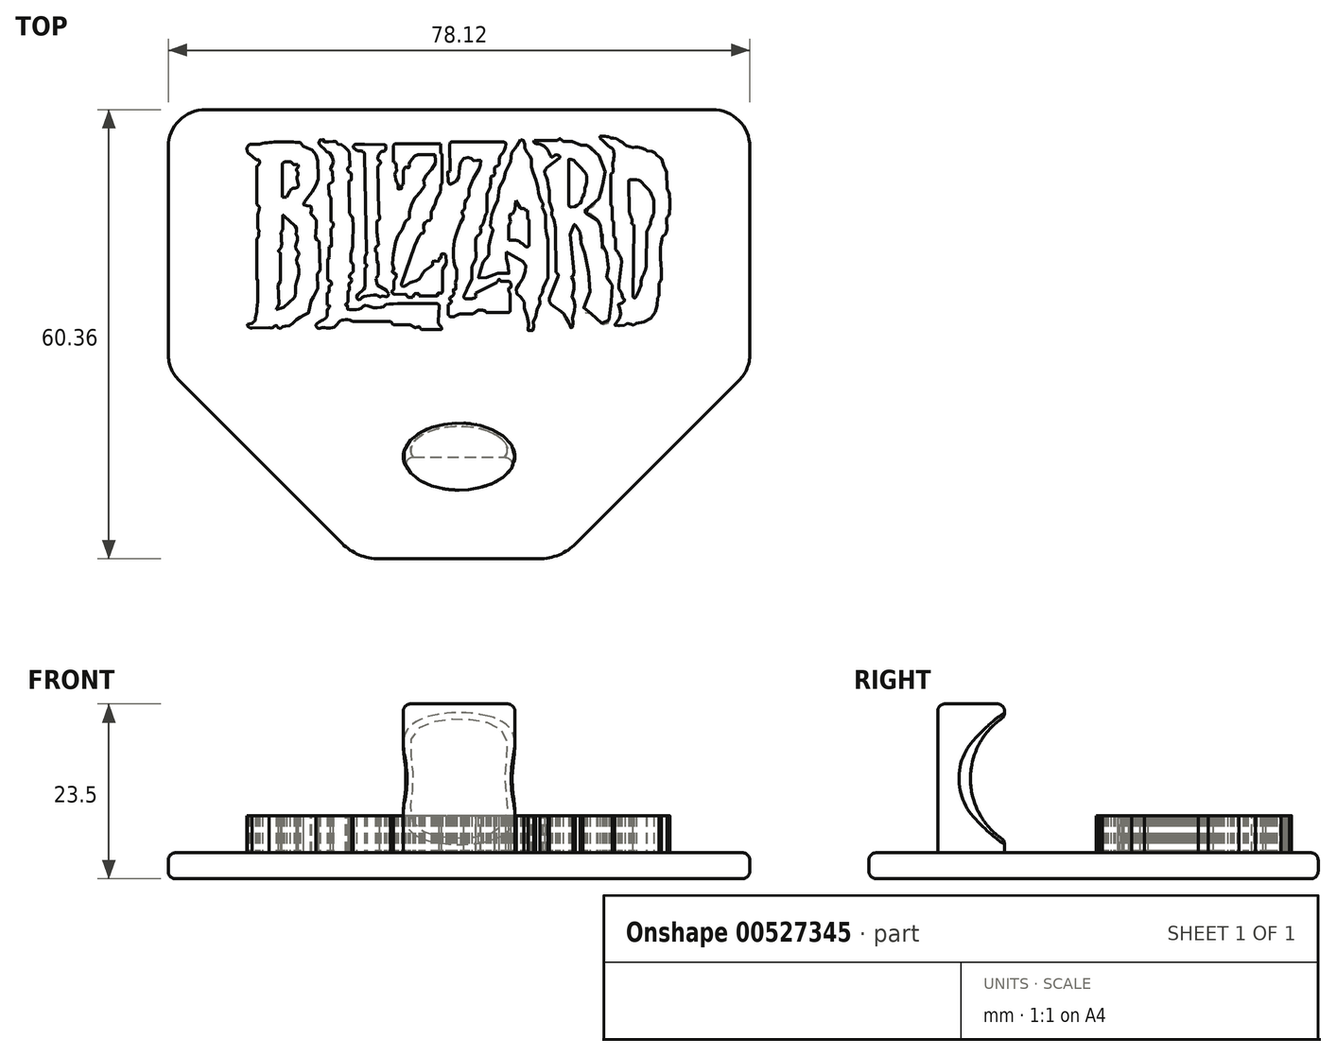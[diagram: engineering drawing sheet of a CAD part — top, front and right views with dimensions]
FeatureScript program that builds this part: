
annotation { "Feature Type Name" : "Feature", "Feature Type Description" : "" }
export const myFeature = defineFeature(function(context is Context, id is Id, definition is map)
    precondition{}
    {
        {
            var Q0;
            Q0=qCreatedBy(makeId("Top.planeOp"),FACE);
            var sketch = newSketch(context, id + "F0", { "sketchPlane" : qUnion([Q0])});
            skLineSegment(sketch, "E0", {"start": v(-31.15, 9.77) * mm, "end": v(-31.15, 4.7) * mm});
            skLineSegment(sketch, "E1", {"start": v(-27.73, 10.06) * mm, "end": v(-27.73, 5.6) * mm});
            skLineSegment(sketch, "E2", {"start": v(-27.56, -9.2) * mm, "end": v(-26.16, -7.94) * mm});
            skLineSegment(sketch, "E3", {"start": v(-16.69, 11.24) * mm, "end": v(-16.4, -1.7) * mm});
            skLineSegment(sketch, "E4", {"start": v(-21.18, 2.33) * mm, "end": v(-21.18, 5.56) * mm});
            skLineSegment(sketch, "E5", {"start": v(-12.42, 12.8) * mm, "end": v(-6.45, 12.8) * mm});
            skLineSegment(sketch, "E6", {"start": v(-5, 13.02) * mm, "end": v(2.01, 13.02) * mm});
            skLineSegment(sketch, "E7", {"start": v(-0.26, -9.88) * mm, "end": v(2.61, -9.88) * mm});
            skLineSegment(sketch, "E8", {"start": v(-12.22, -8.7) * mm, "end": v(-7.01, -8.7) * mm});
            skLineSegment(sketch, "E9", {"start": v(-11.71, -6.1) * mm, "end": v(-9.93, -0.9) * mm});
            skLineSegment(sketch, "E10", {"start": v(-14.92, 9.66) * mm, "end": v(-14.8, 3.49) * mm});
            skLineSegment(sketch, "E11", {"start": v(-9.4, 11.32) * mm, "end": v(-7.37, 11.32) * mm});
            skLineSegment(sketch, "E12", {"start": v(19.53, 1.66) * mm, "end": v(19.41, -7.54) * mm});
            skLineSegment(sketch, "E13", {"start": v(10.74, 10.42) * mm, "end": v(10.74, 4.64) * mm});
            skLineSegment(sketch, "E14", {"start": v(10.93, 0.57) * mm, "end": v(11.43, 1.89) * mm});
            skLineSegment(sketch, "E15", {"start": v(11.61, 1.83) * mm, "end": v(12.27, 0.9) * mm});
            skLineSegment(sketch, "E16", {"start": v(18.97, 7.94) * mm, "end": v(19.83, 7.94) * mm});
            skLineSegment(sketch, "E17", {"start": v(-21.66, -2.75) * mm, "end": v(-21.66, -5.44) * mm});
            skLineSegment(sketch, "E18", {"start": v(-18.23, -3.4) * mm, "end": v(-18.23, -4.42) * mm});
            skLineSegment(sketch, "E19", {"start": v(-27.68, 2.98) * mm, "end": v(-27.68, 1.32) * mm});
            skLineSegment(sketch, "E20", {"start": v(-27.5, 3.09) * mm, "end": v(-26.01, 1.7) * mm});
            skLineSegment(sketch, "E21", {"start": v(-28.3, -6.24) * mm, "end": v(-28.19, -8.73) * mm});
            skLineSegment(sketch, "E22", {"start": v(-28.3, -6.24) * mm, "end": v(-27.98, -5.72) * mm});
            skLineSegment(sketch, "E23", {"start": v(-31.22, 10.62) * mm, "end": v(-32.18, 11.42) * mm});
            skLineSegment(sketch, "E24", {"start": v(-9.07, -12.2) * mm, "end": v(-6.44, -12.2) * mm});
            skLineSegment(sketch, "E25", {"start": v(-6.66, -9.06) * mm, "end": v(-6.8, -11.02) * mm});
            skLineSegment(sketch, "E26", {"start": v(-18.19, -11.12) * mm, "end": v(-13.16, -11.12) * mm});
            skLineSegment(sketch, "E27", {"start": v(-13.16, -11.12) * mm, "end": v(-12.82, -11.53) * mm});
            skLineSegment(sketch, "E28", {"start": v(-12.82, -11.53) * mm, "end": v(-10.6, -11.53) * mm});
            skLineSegment(sketch, "E29", {"start": v(-10.6, -11.53) * mm, "end": v(-9.86, -11.92) * mm});
            skLineSegment(sketch, "E30", {"start": v(-9.22, -11.9) * mm, "end": v(-9.07, -12.2) * mm});
            skLineSegment(sketch, "E31", {"start": v(-21.68, -7.33) * mm, "end": v(-21.68, -8.9) * mm});
            skLineSegment(sketch, "E32", {"start": v(-18.92, -7.07) * mm, "end": v(-18.92, -8.47) * mm});
            skLineSegment(sketch, "E33", {"start": v(-22.76, -0.4) * mm, "end": v(-22.66, -4.23) * mm});
            skLineSegment(sketch, "E34", {"start": v(-21.16, 1.4) * mm, "end": v(-21.1, -0.86) * mm});
            skLineSegment(sketch, "E35", {"start": v(-18.8, 7.77) * mm, "end": v(-18.7, 3.44) * mm});
            skLineSegment(sketch, "E36", {"start": v(-6.26, 11.4) * mm, "end": v(-6.26, 7.46) * mm});
            skLineSegment(sketch, "E37", {"start": v(-5.23, 12.65) * mm, "end": v(-5.16, 9.13) * mm});
            skLineSegment(sketch, "E38", {"start": v(5.45, 2.52) * mm, "end": v(5.45, -0.87) * mm});
            skLineSegment(sketch, "E39", {"start": v(2.68, 1.8) * mm, "end": v(2.68, -0.2) * mm});
            skLineSegment(sketch, "E40", {"start": v(2.68, -0.2) * mm, "end": v(3.72, -0.2) * mm});
            skLineSegment(sketch, "E41", {"start": v(3.67, 5.18) * mm, "end": v(3.55, 3.97) * mm});
            skLineSegment(sketch, "E42", {"start": v(3.67, 5.18) * mm, "end": v(4.2, 4.19) * mm});
            skLineSegment(sketch, "E43", {"start": v(5.24, 3.8) * mm, "end": v(5.24, 2.67) * mm});
            skLineSegment(sketch, "E44", {"start": v(2.95, 3.31) * mm, "end": v(3.2, 3.31) * mm});
            skLineSegment(sketch, "E45", {"start": v(2.81, 2.88) * mm, "end": v(2.93, 2.3) * mm});
            skLineSegment(sketch, "E46", {"start": v(2.93, 2.3) * mm, "end": v(2.68, 1.8) * mm});
            skLineSegment(sketch, "E47", {"start": v(4.5, -0.62) * mm, "end": v(4.93, -1) * mm});
            skArc(sketch, "E48", {"start": v(4.93, -1) * mm, "mid": v(5.22, -1.07) * mm, "end": v(5.45, -0.87) * mm});
            skFitSpline(sketch, "E49", {"points": [v(3.72, -0.2) * mm, v(3.88, -0.24) * mm, v(4.03, -0.29) * mm, v(4.16, -0.37) * mm, v(4.22, -0.48) * mm, v(4.26, -0.54) * mm, v(4.34, -0.57) * mm, v(4.5, -0.62) * mm], "startDerivative": vector(1.01, -0.19) * mm, "endDerivative": vector(1.05, -0.37) * mm});
            skFitSpline(sketch, "E50", {"points": [v(2.95, 3.31) * mm, v(2.89, 3.31) * mm, v(2.84, 3.27) * mm, v(2.82, 3.17) * mm, v(2.81, 2.88) * mm], "startDerivative": vector(-0.37, 0.05) * mm, "endDerivative": vector(0, -0.8) * mm});
            skLineSegment(sketch, "E51", {"start": v(3.55, 3.97) * mm, "end": v(3.2, 3.31) * mm});
            skLineSegment(sketch, "E52", {"start": v(4.41, 4.08) * mm, "end": v(4.78, 4.08) * mm});
            skLineSegment(sketch, "E53", {"start": v(4.78, 4.08) * mm, "end": v(4.98, 3.8) * mm});
            skLineSegment(sketch, "E54", {"start": v(4.98, 3.8) * mm, "end": v(5.24, 3.8) * mm});
            skArc(sketch, "E55", {"start": v(4.2, 4.19) * mm, "mid": v(4.29, 4.1) * mm, "end": v(4.41, 4.08) * mm});
            skLineSegment(sketch, "E56", {"start": v(-27.73, 5.6) * mm, "end": v(-27.17, 5.6) * mm});
            skLineSegment(sketch, "E57", {"start": v(-27.17, 5.6) * mm, "end": v(-26.68, 6.45) * mm});
            skFitSpline(sketch, "E58", {"points": [v(-26.68, 6.45) * mm, v(-26.55, 6.63) * mm, v(-26.38, 6.75) * mm, v(-26.2, 6.8) * mm, v(-25.95, 6.83) * mm, v(-25.75, 6.87) * mm, v(-25.62, 6.99) * mm, v(-25.58, 7.26) * mm, v(-25.66, 7.62) * mm, v(-25.75, 7.96) * mm, v(-25.76, 8.33) * mm, v(-25.66, 8.45) * mm, v(-25.6, 8.59) * mm, v(-25.6, 8.77) * mm, v(-25.64, 8.96) * mm, v(-25.75, 9.1) * mm, v(-25.83, 9.18) * mm, v(-25.83, 9.37) * mm, v(-25.69, 9.54) * mm, v(-25.57, 9.7) * mm, v(-25.55, 9.87) * mm, v(-25.65, 9.97) * mm], "startDerivative": vector(2.6, 3.85) * mm, "endDerivative": vector(-3.2, 2.1) * mm});
            skLineSegment(sketch, "E59", {"start": v(-25.65, 9.97) * mm, "end": v(-26.14, 9.97) * mm});
            skFitSpline(sketch, "E60", {"points": [v(-26.14, 9.97) * mm, v(-26.21, 9.97) * mm, v(-26.32, 10.06) * mm, v(-26.37, 10.19) * mm, v(-26.5, 10.31) * mm, v(-26.68, 10.34) * mm, v(-27.42, 10.33) * mm, v(-27.52, 10.31) * mm, v(-27.63, 10.25) * mm, v(-27.7, 10.16) * mm, v(-27.73, 10.06) * mm], "startDerivative": vector(-1.06, -0.2) * mm, "endDerivative": vector(-0.35, -1.25) * mm});
            skFitSpline(sketch, "E61", {"points": [v(-27.68, 2.98) * mm, v(-27.68, 3.09) * mm, v(-27.68, 3.16) * mm, v(-27.62, 3.2) * mm, v(-27.57, 3.18) * mm, v(-27.52, 3.14) * mm, v(-27.5, 3.09) * mm], "startDerivative": vector(0.02, 0.53) * mm, "endDerivative": vector(0.13, -0.34) * mm});
            skFitSpline(sketch, "E62", {"points": [v(-27.68, 1.32) * mm, v(-27.73, 1.12) * mm, v(-27.85, 0.93) * mm, v(-27.92, 0.81) * mm, v(-27.89, 0.53) * mm, v(-27.85, 0.23) * mm, v(-27.83, 0) * mm, v(-27.83, -0.4) * mm, v(-27.82, -0.75) * mm, v(-27.86, -1.16) * mm], "startDerivative": vector(-0.36, -2.08) * mm, "endDerivative": vector(-0.44, -3.06) * mm});
            skLineSegment(sketch, "E63", {"start": v(-27.86, -1.16) * mm, "end": v(-28.16, -1.5) * mm});
            skFitSpline(sketch, "E64", {"points": [v(-28.16, -1.5) * mm, v(-28.22, -1.56) * mm, v(-28.22, -1.63) * mm, v(-28.16, -1.76) * mm, v(-28.08, -1.85) * mm, v(-28, -1.92) * mm], "startDerivative": vector(-0.41, -0.35) * mm, "endDerivative": vector(0.38, -0.36) * mm});
            skLineSegment(sketch, "E65", {"start": v(-28, -1.92) * mm, "end": v(-27.98, -5.72) * mm});
            skLineSegment(sketch, "E66", {"start": v(-28.19, -8.73) * mm, "end": v(-28.57, -9.51) * mm});
            skLineSegment(sketch, "E67", {"start": v(-28.57, -9.51) * mm, "end": v(-27.56, -9.2) * mm});
            skFitSpline(sketch, "E68", {"points": [v(-26.01, 1.7) * mm, v(-25.88, 1.58) * mm, v(-25.82, 1.44) * mm, v(-25.81, 1.19) * mm, v(-25.86, 0.99) * mm, v(-25.87, 0.81) * mm, v(-25.85, 0.56) * mm, v(-25.75, 0.36) * mm, v(-25.68, 0.07) * mm, v(-25.69, -0.19) * mm, v(-25.75, -0.44) * mm, v(-25.85, -0.68) * mm, v(-25.92, -0.92) * mm, v(-25.93, -1.18) * mm, v(-25.87, -1.41) * mm, v(-25.65, -1.7) * mm, v(-25.46, -1.92) * mm, v(-25.46, -2.03) * mm, v(-25.54, -2.18) * mm, v(-25.68, -2.42) * mm, v(-25.76, -2.65) * mm, v(-25.81, -2.87) * mm, v(-25.82, -3.08) * mm, v(-25.72, -3.32) * mm, v(-25.58, -3.65) * mm, v(-25.5, -4) * mm, v(-25.49, -4.34) * mm, v(-25.53, -4.68) * mm, v(-25.65, -5.2) * mm, v(-25.77, -5.7) * mm, v(-25.9, -6.15) * mm, v(-25.94, -6.41) * mm, v(-25.95, -6.77) * mm, v(-25.95, -7.07) * mm, v(-25.97, -7.37) * mm, v(-26.01, -7.63) * mm, v(-26.05, -7.75) * mm, v(-26.1, -7.83) * mm, v(-26.16, -7.94) * mm], "startDerivative": vector(6.73, -5.57) * mm, "endDerivative": vector(-2.82, -6.3) * mm});
            skLineSegment(sketch, "E69", {"start": v(-31.06, 3.12) * mm, "end": v(-31.06, 1.5) * mm});
            skLineSegment(sketch, "E70", {"start": v(-31.14, 0) * mm, "end": v(-31.14, -5.33) * mm});
            skFitSpline(sketch, "E71", {"points": [v(-31.15, 4.7) * mm, v(-31.03, 4.5) * mm, v(-30.83, 4.3) * mm, v(-30.84, 3.95) * mm, v(-30.97, 3.48) * mm, v(-31.06, 3.12) * mm], "startDerivative": vector(0.56, -1.18) * mm, "endDerivative": vector(-0.38, -1.64) * mm});
            skFitSpline(sketch, "E72", {"points": [v(-31.06, 1.5) * mm, v(-30.98, 1.32) * mm, v(-30.9, 1.2) * mm, v(-30.86, 1.02) * mm, v(-30.88, 0.85) * mm, v(-30.89, 0.63) * mm, v(-30.94, 0.28) * mm, v(-31.14, 0) * mm], "startDerivative": vector(0.55, -1.52) * mm, "endDerivative": vector(-1.3, -1.44) * mm});
            skFitSpline(sketch, "E73", {"points": [v(-31.22, 10.62) * mm, v(-31.06, 10.62) * mm, v(-30.9, 10.62) * mm, v(-30.81, 10.47) * mm, v(-30.8, 10.2) * mm, v(-30.86, 9.98) * mm, v(-31.01, 9.86) * mm, v(-31.15, 9.77) * mm], "startDerivative": vector(1.2, -0.07) * mm, "endDerivative": vector(-0.95, -0.73) * mm});
            skFitSpline(sketch, "E74", {"points": [v(-32.18, 11.42) * mm, v(-32.39, 11.65) * mm, v(-32.47, 11.95) * mm, v(-32.46, 12.25) * mm, v(-32.4, 12.4) * mm, v(-32.18, 12.65) * mm, v(-31.88, 12.73) * mm], "startDerivative": vector(-1.35, 1.27) * mm, "endDerivative": vector(1.83, 0.17) * mm});
            skLineSegment(sketch, "E75", {"start": v(-31.88, 12.73) * mm, "end": v(-30.79, 12.73) * mm});
            skLineSegment(sketch, "E76", {"start": v(-30.79, 12.73) * mm, "end": v(-30.42, 12.87) * mm});
            skLineSegment(sketch, "E77", {"start": v(-25.33, 12.95) * mm, "end": v(-24.9, 12.43) * mm});
            skArc(sketch, "E78", {"start": v(-25.33, 12.95) * mm, "mid": v(-27.88, 13.03) * mm, "end": v(-30.42, 12.87) * mm});
            skFitSpline(sketch, "E79", {"points": [v(-24.9, 12.43) * mm, v(-24.63, 12.3) * mm, v(-24.19, 12.19) * mm, v(-23.73, 11.98) * mm, v(-23.3, 11.4) * mm, v(-23, 10.67) * mm, v(-23, 9.96) * mm, v(-22.97, 9.6) * mm, v(-22.88, 8.55) * mm, v(-22.97, 7.72) * mm, v(-23.38, 6.91) * mm, v(-23.94, 6.02) * mm, v(-24.32, 5.5) * mm, v(-24.78, 4.9) * mm, v(-24.86, 4.73) * mm, v(-24.86, 4.58) * mm, v(-24.75, 4.5) * mm, v(-24.46, 4.46) * mm, v(-24.13, 4.45) * mm, v(-23.89, 4.37) * mm, v(-23.78, 4.15) * mm, v(-23.79, 3.88) * mm, v(-23.87, 3.56) * mm, v(-23.88, 3.26) * mm, v(-23.67, 3.03) * mm, v(-23.2, 2.7) * mm, v(-23.14, 2.29) * mm, v(-23.18, 1.69) * mm, v(-23.25, 0.83) * mm, v(-23.26, 0.22) * mm, v(-23.26, 0.12) * mm, v(-23.24, 0) * mm, v(-23.06, -0.14) * mm, v(-22.9, -0.25) * mm, v(-22.76, -0.4) * mm], "startDerivative": vector(10.18, -5.43) * mm, "endDerivative": vector(6.5, -7.56) * mm});
            skFitSpline(sketch, "E80", {"points": [v(-31.14, -5.33) * mm, v(-31.04, -5.7) * mm, v(-31.03, -6.29) * mm, v(-31, -7.35) * mm, v(-31.05, -8.3) * mm, v(-31.14, -9.37) * mm, v(-31.2, -9.97) * mm, v(-31.24, -10.15) * mm, v(-31.33, -10.39) * mm, v(-31.33, -10.6) * mm, v(-31.35, -10.82) * mm, v(-31.41, -11) * mm, v(-31.58, -11.16) * mm, v(-31.82, -11.33) * mm, v(-32.11, -11.4) * mm, v(-32.39, -11.5) * mm, v(-32.42, -11.66) * mm, v(-32.28, -11.83) * mm, v(-32.03, -11.97) * mm, v(-31.77, -12) * mm], "startDerivative": vector(2.24, -6.72) * mm, "endDerivative": vector(5.9, -0.17) * mm});
            skLineSegment(sketch, "E81", {"start": v(-31.77, -12) * mm, "end": v(-29.5, -11.93) * mm});
            skFitSpline(sketch, "E82", {"points": [v(-29.5, -11.93) * mm, v(-29.36, -11.93) * mm, v(-29.27, -11.97) * mm, v(-29.17, -12) * mm, v(-29.05, -12) * mm, v(-29, -11.93) * mm, v(-28.8, -11.74) * mm, v(-28.7, -11.65) * mm, v(-28.57, -11.62) * mm, v(-28.43, -11.68) * mm, v(-28.32, -11.8) * mm, v(-28.23, -11.97) * mm, v(-28.08, -12.04) * mm, v(-27.94, -11.98) * mm, v(-27.7, -11.83) * mm, v(-27.51, -11.72) * mm, v(-27.36, -11.71) * mm, v(-26.84, -11.7) * mm, v(-26.43, -11.44) * mm, v(-25.93, -10.95) * mm, v(-25.38, -10.55) * mm, v(-24.88, -10.28) * mm, v(-24.27, -10) * mm, v(-24.21, -9.92) * mm, v(-24.05, -9.37) * mm, v(-23.96, -8.8) * mm, v(-23.83, -8.28) * mm, v(-23.59, -7.82) * mm, v(-23.17, -7.12) * mm, v(-22.99, -6.7) * mm, v(-22.96, -6.17) * mm, v(-23, -5.3) * mm, v(-23.03, -4.7) * mm], "startDerivative": vector(7.6, 0.68) * mm, "endDerivative": vector(-0.7, 13.38) * mm});
            skLineSegment(sketch, "E83", {"start": v(-23.03, -4.7) * mm, "end": v(-22.66, -4.23) * mm});
            skLineSegment(sketch, "E84", {"start": v(-15.23, -1.21) * mm, "end": v(-15.23, -1.67) * mm});
            skLineSegment(sketch, "E85", {"start": v(-15.23, -1.67) * mm, "end": v(-15.03, -1.84) * mm});
            skLineSegment(sketch, "E86", {"start": v(-15.03, -1.84) * mm, "end": v(-15.02, -2.98) * mm});
            skLineSegment(sketch, "E87", {"start": v(-15.02, -2.98) * mm, "end": v(-14.83, -3.3) * mm});
            skLineSegment(sketch, "E88", {"start": v(-14.83, -3.3) * mm, "end": v(-14.82, -4.85) * mm});
            skLineSegment(sketch, "E89", {"start": v(-14.82, -4.85) * mm, "end": v(-15.15, -5.3) * mm});
            skLineSegment(sketch, "E90", {"start": v(-15.15, -5.3) * mm, "end": v(-15, -6.24) * mm});
            skLineSegment(sketch, "E91", {"start": v(-15, -6.24) * mm, "end": v(-13.75, -6.92) * mm});
            skLineSegment(sketch, "E92", {"start": v(-16.64, -6.44) * mm, "end": v(-16.6, -3.93) * mm});
            skLineSegment(sketch, "E93", {"start": v(-16.61, -3.31) * mm, "end": v(-16.61, -2.45) * mm});
            skLineSegment(sketch, "E94", {"start": v(-15.03, 2.4) * mm, "end": v(-15.03, 1.05) * mm});
            skLineSegment(sketch, "E95", {"start": v(-21.52, 7.32) * mm, "end": v(-21.46, 5.83) * mm});
            skLineSegment(sketch, "E96", {"start": v(-21.52, 7.32) * mm, "end": v(-20.95, 7.67) * mm});
            skLineSegment(sketch, "E97", {"start": v(-20.97, 9.09) * mm, "end": v(-20.95, 7.67) * mm});
            skLineSegment(sketch, "E98", {"start": v(-18.7, 11.39) * mm, "end": v(-18.66, 9.67) * mm});
            skLineSegment(sketch, "E99", {"start": v(-1.75, -7.32) * mm, "end": v(1.04, -5.92) * mm});
            skLineSegment(sketch, "E100", {"start": v(1.68, -5.68) * mm, "end": v(2.76, -5.68) * mm});
            skLineSegment(sketch, "E101", {"start": v(2.9, -7.35) * mm, "end": v(2.9, -9.62) * mm});
            skLineSegment(sketch, "E102", {"start": v(-3.81, -10.09) * mm, "end": v(-2.26, -10.09) * mm});
            skLineSegment(sketch, "E103", {"start": v(-5.44, -8.79) * mm, "end": v(-5.44, -10.1) * mm});
            skLineSegment(sketch, "E104", {"start": v(-2.29, -5.41) * mm, "end": v(-2.9, -6.7) * mm});
            skLineSegment(sketch, "E105", {"start": v(-3.02, -7.06) * mm, "end": v(-3.26, -7.56) * mm});
            skLineSegment(sketch, "E106", {"start": v(2.4, -1.8) * mm, "end": v(4.59, -3.02) * mm});
            skLineSegment(sketch, "E107", {"start": v(9.3, -5.1) * mm, "end": v(8.14, -7.99) * mm});
            skLineSegment(sketch, "E108", {"start": v(9.02, -4.44) * mm, "end": v(8.95, 1.3) * mm});
            skLineSegment(sketch, "E109", {"start": v(8, 9.73) * mm, "end": v(9.43, 10.8) * mm});
            skLineSegment(sketch, "E110", {"start": v(11.22, 13.08) * mm, "end": v(12.41, 12.57) * mm});
            skLineSegment(sketch, "E111", {"start": v(12.41, 12.57) * mm, "end": v(13.22, 12.56) * mm});
            skLineSegment(sketch, "E112", {"start": v(6.1, 13.21) * mm, "end": v(9.16, 13.21) * mm});
            skLineSegment(sketch, "E113", {"start": v(11.22, 13.08) * mm, "end": v(10, 13.08) * mm});
            skLineSegment(sketch, "E114", {"start": v(16.4, 8.71) * mm, "end": v(16.4, 4.5) * mm});
            skLineSegment(sketch, "E115", {"start": v(16.4, 4.5) * mm, "end": v(16.6, 4.31) * mm});
            skLineSegment(sketch, "E116", {"start": v(16.6, 4.31) * mm, "end": v(16.6, 2.47) * mm});
            skLineSegment(sketch, "E117", {"start": v(16.6, 2.47) * mm, "end": v(16.76, 2.28) * mm});
            skLineSegment(sketch, "E118", {"start": v(16.76, 2.28) * mm, "end": v(16.76, 0.36) * mm});
            skLineSegment(sketch, "E119", {"start": v(16.76, 0.36) * mm, "end": v(17.05, 0.1) * mm});
            skLineSegment(sketch, "E120", {"start": v(17.05, 0.1) * mm, "end": v(17.05, -1.14) * mm});
            skLineSegment(sketch, "E121", {"start": v(17.5, -6.18) * mm, "end": v(17.86, -3.1) * mm});
            skLineSegment(sketch, "E122", {"start": v(22.9, -7.67) * mm, "end": v(22.9, -5.97) * mm});
            skLineSegment(sketch, "E123", {"start": v(23.92, 2.6) * mm, "end": v(23.98, 1.29) * mm});
            skLineSegment(sketch, "E124", {"start": v(23.9, 8.97) * mm, "end": v(23.95, 6.74) * mm});
            skLineSegment(sketch, "E125", {"start": v(21.24, 0.97) * mm, "end": v(21.19, -3.56) * mm});
            skFitSpline(sketch, "E126", {"points": [v(-20.97, 9.09) * mm, v(-21.16, 9.2) * mm, v(-21.25, 9.38) * mm, v(-21.21, 9.57) * mm, v(-21.1, 9.73) * mm, v(-20.97, 9.95) * mm, v(-20.86, 10.21) * mm, v(-20.92, 10.86) * mm, v(-21.16, 11.1) * mm, v(-21.22, 11.4) * mm, v(-21.32, 11.53) * mm, v(-21.65, 11.6) * mm, v(-21.93, 11.9) * mm, v(-22.16, 12.18) * mm, v(-22.65, 12.56) * mm, v(-22.81, 12.9) * mm, v(-22.66, 13.3) * mm, v(-22.34, 13.4) * mm, v(-22.1, 13.2) * mm, v(-22.05, 13) * mm, v(-21.49, 13.02) * mm, v(-20.9, 13.09) * mm, v(-20.58, 13.09) * mm, v(-20.34, 12.9) * mm, v(-20.16, 12.67) * mm, v(-19.66, 12.67) * mm, v(-19.34, 12.34) * mm, v(-19.08, 12.07) * mm, v(-18.87, 11.85) * mm, v(-18.73, 11.6) * mm, v(-18.7, 11.39) * mm], "startDerivative": vector(-7.54, 3.68) * mm, "endDerivative": vector(1.1, -7.65) * mm});
            skPoint(sketch, "E127.1.internal.snap0", {"position": v(-18.75, 5.6) * mm});
            skFitSpline(sketch, "E127", {"points": [v(-18.66, 9.67) * mm, v(-18.75, 9.64) * mm, v(-18.87, 9.59) * mm, v(-18.94, 9.5) * mm, v(-18.93, 9.26) * mm, v(-18.87, 9.09) * mm, v(-18.78, 8.96) * mm, v(-18.62, 8.91) * mm, v(-18.52, 8.82) * mm, v(-18.45, 8.6) * mm, v(-18.44, 8.33) * mm, v(-18.44, 8.06) * mm, v(-18.51, 7.9) * mm, v(-18.66, 7.82) * mm, v(-18.8, 7.77) * mm], "startDerivative": vector(-1.5, -0.64) * mm, "endDerivative": vector(-1.9, -0.63) * mm});
            skFitSpline(sketch, "E128", {"points": [v(-21.18, 2.33) * mm, v(-20.97, 2.21) * mm, v(-20.86, 2.04) * mm, v(-20.88, 1.8) * mm, v(-20.97, 1.55) * mm, v(-21.16, 1.4) * mm], "startDerivative": vector(1.1, -0.55) * mm, "endDerivative": vector(-1.08, -0.61) * mm});
            skFitSpline(sketch, "E129", {"points": [v(-18.7, 3.44) * mm, v(-18.52, 3.14) * mm, v(-18.32, 3) * mm, v(-18.28, 2.76) * mm, v(-18.22, 2.03) * mm, v(-18.21, 1.16) * mm, v(-18.27, -0.45) * mm, v(-18.32, -1.3) * mm, v(-18.45, -1.68) * mm, v(-18.51, -1.94) * mm, v(-18.51, -2.33) * mm, v(-18.51, -2.75) * mm, v(-18.51, -3.06) * mm, v(-18.23, -3.4) * mm], "startDerivative": vector(2.35, -5.3) * mm, "endDerivative": vector(5.02, -4.56) * mm});
            skFitSpline(sketch, "E130", {"points": [v(-21.1, -0.86) * mm, v(-21.1, -0.95) * mm, v(-21.2, -0.98) * mm, v(-21.32, -1) * mm, v(-21.46, -1.12) * mm, v(-21.46, -1.28) * mm, v(-21.42, -1.97) * mm, v(-21.43, -2.32) * mm, v(-21.41, -2.56) * mm, v(-21.52, -2.63) * mm, v(-21.6, -2.67) * mm, v(-21.66, -2.75) * mm], "startDerivative": vector(0.35, -1.61) * mm, "endDerivative": vector(-0.77, -1.42) * mm});
            skFitSpline(sketch, "E131", {"points": [v(-21.66, -5.44) * mm, v(-21.53, -5.58) * mm, v(-21.3, -5.68) * mm, v(-21.1, -5.84) * mm, v(-21.1, -6.07) * mm, v(-21.1, -6.2) * mm, v(-21.27, -6.27) * mm, v(-21.4, -6.31) * mm, v(-21.44, -6.41) * mm, v(-21.42, -6.63) * mm, v(-21.42, -6.84) * mm, v(-21.42, -7.09) * mm, v(-21.53, -7.19) * mm, v(-21.68, -7.33) * mm], "startDerivative": vector(1.37, -2.06) * mm, "endDerivative": vector(-1.74, -1.99) * mm});
            skFitSpline(sketch, "E132", {"points": [v(-21.68, -8.9) * mm, v(-21.56, -8.96) * mm, v(-21.43, -8.95) * mm, v(-21.37, -9) * mm, v(-21.35, -9.12) * mm, v(-21.4, -9.23) * mm, v(-21.51, -9.3) * mm, v(-21.63, -9.4) * mm, v(-21.66, -9.48) * mm, v(-21.68, -10.16) * mm, v(-21.68, -10.31) * mm, v(-21.72, -10.43) * mm, v(-21.84, -10.57) * mm, v(-22.06, -10.76) * mm, v(-22.44, -11) * mm, v(-22.79, -11.18) * mm, v(-23.04, -11.38) * mm, v(-23.19, -11.51) * mm], "startDerivative": vector(2.37, -1.82) * mm, "endDerivative": vector(-2.29, -2.21) * mm});
            skFitSpline(sketch, "E133", {"points": [v(-18.23, -4.42) * mm, v(-18.53, -4.68) * mm, v(-18.7, -4.98) * mm, v(-18.68, -5.17) * mm, v(-18.57, -5.3) * mm, v(-18.43, -5.39) * mm, v(-18.43, -5.62) * mm, v(-18.5, -5.81) * mm, v(-18.63, -5.9) * mm, v(-18.75, -5.97) * mm, v(-18.75, -6.18) * mm, v(-18.75, -6.44) * mm, v(-18.7, -6.68) * mm, v(-18.7, -6.9) * mm, v(-18.75, -6.98) * mm, v(-18.85, -7) * mm, v(-18.92, -7.07) * mm], "startDerivative": vector(-3.61, -2.63) * mm, "endDerivative": vector(-1.31, -1.97) * mm});
            skFitSpline(sketch, "E134", {"points": [v(-18.92, -8.47) * mm, v(-18.97, -8.57) * mm, v(-19.08, -8.66) * mm, v(-19.2, -8.78) * mm, v(-19.25, -8.85) * mm, v(-19.2, -8.94) * mm, v(-19.03, -8.95) * mm, v(-18.96, -9) * mm, v(-18.96, -9.2) * mm, v(-18.98, -9.31) * mm, v(-18.98, -9.44) * mm, v(-18.79, -9.48) * mm, v(-18.33, -9.53) * mm, v(-17.92, -9.53) * mm, v(-17.5, -9.48) * mm, v(-17.26, -9.4) * mm, v(-16.92, -9.1) * mm, v(-16.72, -8.94) * mm, v(-16.46, -8.94) * mm, v(-16.1, -9.06) * mm, v(-15.65, -9.23) * mm, v(-15.12, -9.25) * mm, v(-14.42, -9.2) * mm, v(-14.15, -9.1) * mm, v(-13.77, -8.8) * mm, v(-13.12, -8.73) * mm, v(-12.22, -8.7) * mm], "startDerivative": vector(-1.59, -4.44) * mm, "endDerivative": vector(13.73, 0.52) * mm});
            skFitSpline(sketch, "E135", {"points": [v(-7.01, -8.7) * mm, v(-6.83, -8.73) * mm, v(-6.69, -8.86) * mm, v(-6.66, -9.06) * mm], "startDerivative": vector(0.56, -0.04) * mm, "endDerivative": vector(-0.01, -0.64) * mm});
            skFitSpline(sketch, "E136", {"points": [v(-6.8, -11.02) * mm, v(-6.76, -11.28) * mm, v(-6.7, -11.44) * mm, v(-6.54, -11.63) * mm, v(-6.37, -11.86) * mm, v(-6.31, -12.05) * mm, v(-6.31, -12.14) * mm, v(-6.44, -12.2) * mm], "startDerivative": vector(0.23, -1.64) * mm, "endDerivative": vector(-1.3, -0.34) * mm});
            skFitSpline(sketch, "E137", {"points": [v(-9.86, -11.92) * mm, v(-9.62, -11.88) * mm, v(-9.45, -11.83) * mm, v(-9.36, -11.8) * mm, v(-9.26, -11.87) * mm, v(-9.22, -11.9) * mm], "startDerivative": vector(0.9, 0.17) * mm, "endDerivative": vector(0.24, -0.23) * mm});
            skFitSpline(sketch, "E138", {"points": [v(-23.19, -11.51) * mm, v(-23.19, -11.7) * mm, v(-23.05, -11.9) * mm, v(-22.8, -12.04) * mm, v(-22.6, -12) * mm, v(-22.36, -11.92) * mm, v(-22.1, -11.92) * mm, v(-21.8, -11.98) * mm, v(-21.45, -11.98) * mm, v(-20.9, -11.92) * mm, v(-20.55, -11.67) * mm, v(-20.2, -11.26) * mm, v(-19.87, -10.97) * mm, v(-19.47, -10.87) * mm, v(-18.88, -10.88) * mm, v(-18.4, -11.02) * mm], "startDerivative": vector(-0.54, -3.95) * mm, "endDerivative": vector(5.75, -2.22) * mm});
            skFitSpline(sketch, "E139", {"points": [v(-18.4, -11.02) * mm, v(-18.19, -11.12) * mm], "startDerivative": vector(0.22, -0.1) * mm, "endDerivative": vector(0.22, -0.1) * mm});
            skFitSpline(sketch, "E140", {"points": [v(-16.64, -6.44) * mm, v(-16.86, -6.88) * mm, v(-17.14, -7.07) * mm, v(-17.44, -7.33) * mm, v(-17.7, -7.63) * mm, v(-17.73, -7.93) * mm, v(-17.57, -8.11) * mm, v(-17.48, -8.2) * mm, v(-17.24, -8.15) * mm, v(-16.97, -7.86) * mm, v(-16.74, -7.7) * mm, v(-16.23, -7.66) * mm, v(-15.65, -7.57) * mm, v(-15.03, -7.58) * mm, v(-14.83, -7.68) * mm, v(-14.58, -7.82) * mm, v(-14.33, -7.7) * mm, v(-13.98, -7.72) * mm, v(-13.74, -7.79) * mm, v(-13.51, -7.66) * mm, v(-13.45, -7.46) * mm, v(-13.51, -7.2) * mm, v(-13.65, -7.07) * mm, v(-13.75, -6.92) * mm], "startDerivative": vector(-3.5, -9.36) * mm, "endDerivative": vector(-2.93, 4.72) * mm});
            skFitSpline(sketch, "E141", {"points": [v(-16.61, -3.31) * mm, v(-16.46, -3.42) * mm, v(-16.38, -3.56) * mm, v(-16.44, -3.72) * mm, v(-16.6, -3.93) * mm], "startDerivative": vector(0.64, -0.43) * mm, "endDerivative": vector(-0.54, -0.73) * mm});
            skFitSpline(sketch, "E142", {"points": [v(-16.4, -1.7) * mm, v(-16.4, -1.93) * mm, v(-16.48, -2.15) * mm, v(-16.56, -2.31) * mm, v(-16.61, -2.45) * mm], "startDerivative": vector(0.1, -0.88) * mm, "endDerivative": vector(-0.24, -0.63) * mm});
            skFitSpline(sketch, "E143", {"points": [v(-14.8, 3.49) * mm, v(-14.7, 3.15) * mm, v(-14.63, 2.86) * mm, v(-14.7, 2.6) * mm, v(-15.03, 2.4) * mm], "startDerivative": vector(0.3, -1.33) * mm, "endDerivative": vector(-1.42, -0.63) * mm});
            skFitSpline(sketch, "E144", {"points": [v(-15.03, 1.05) * mm, v(-14.78, -0.74) * mm, v(-14.65, -1.03) * mm], "startDerivative": vector(0.33, -3.09) * mm, "endDerivative": vector(0.44, -0.75) * mm});
            skFitSpline(sketch, "E145", {"points": [v(-14.92, 9.66) * mm, v(-14.78, 9.87) * mm, v(-14.63, 10.04) * mm, v(-14.54, 10.21) * mm, v(-14.62, 10.45) * mm, v(-14.83, 10.6) * mm, v(-14.87, 10.9) * mm, v(-14.84, 11.17) * mm, v(-14.68, 11.4) * mm, v(-14.48, 11.66) * mm, v(-14.29, 11.77) * mm, v(-13.98, 11.85) * mm, v(-13.84, 12.05) * mm, v(-13.8, 12.3) * mm, v(-13.8, 12.56) * mm, v(-14.02, 12.68) * mm], "startDerivative": vector(2.02, 3.3) * mm, "endDerivative": vector(-3.96, 1.41) * mm});
            skLineSegment(sketch, "E146", {"start": v(-14.02, 12.68) * mm, "end": v(-16.67, 12.74) * mm});
            skLineSegment(sketch, "E147", {"start": v(-16.67, 12.74) * mm, "end": v(-17.76, 12.74) * mm});
            skFitSpline(sketch, "E148", {"points": [v(-17.76, 12.74) * mm, v(-18, 12.65) * mm, v(-18.17, 12.47) * mm, v(-18.16, 12.25) * mm, v(-17.95, 12.08) * mm, v(-17.67, 11.87) * mm, v(-17.4, 11.8) * mm, v(-17.06, 11.8) * mm, v(-16.85, 11.7) * mm, v(-16.67, 11.5) * mm, v(-16.69, 11.24) * mm], "startDerivative": vector(-2.6, -0.71) * mm, "endDerivative": vector(-0.65, -2.74) * mm});
            skLineSegment(sketch, "E149", {"start": v(-12.8, 10.33) * mm, "end": v(-12.8, 12.44) * mm});
            skArc(sketch, "E150", {"start": v(-12.42, 12.8) * mm, "mid": v(-12.69, 12.7) * mm, "end": v(-12.8, 12.44) * mm});
            skFitSpline(sketch, "E151", {"points": [v(-12.8, 10.33) * mm, v(-12.78, 10.28) * mm, v(-12.68, 10.27) * mm, v(-12.55, 10.24) * mm, v(-12.47, 10.11) * mm, v(-12.42, 9.81) * mm, v(-12.4, 9.1) * mm, v(-12.5, 8.96) * mm, v(-12.59, 8.8) * mm, v(-12.54, 8.41) * mm, v(-12.38, 7.63) * mm, v(-12.2, 7.33) * mm, v(-12.16, 7.05) * mm, v(-12.17, 6.72) * mm, v(-12, 6.7) * mm, v(-11.77, 6.72) * mm, v(-11.67, 6.81) * mm, v(-11.71, 6.96) * mm, v(-11.74, 7.12) * mm, v(-11.64, 7.26) * mm, v(-11.47, 7.33) * mm], "startDerivative": vector(0.62, -2.35) * mm, "endDerivative": vector(3.86, 1.35) * mm});
            skLineSegment(sketch, "E152", {"start": v(-11.47, 7.33) * mm, "end": v(-11.47, 9.04) * mm});
            skFitSpline(sketch, "E153", {"points": [v(-11.47, 9.04) * mm, v(-11.45, 9.21) * mm, v(-11.37, 9.4) * mm, v(-11.3, 9.52) * mm, v(-11.17, 9.62) * mm, v(-11.04, 9.63) * mm, v(-10.92, 9.59) * mm, v(-10.78, 9.56) * mm, v(-10.66, 9.66) * mm, v(-10.67, 9.8) * mm, v(-10.66, 10.15) * mm, v(-10.51, 10.45) * mm, v(-10.26, 10.8) * mm, v(-10, 11.05) * mm, v(-9.76, 11.21) * mm, v(-9.54, 11.32) * mm, v(-9.4, 11.32) * mm], "startDerivative": vector(0.13, 3.07) * mm, "endDerivative": vector(2.7, -0.19) * mm});
            skFitSpline(sketch, "E154", {"points": [v(-7.37, 11.32) * mm, v(-7.31, 11.32) * mm, v(-7.25, 11.3) * mm, v(-7.23, 11.22) * mm, v(-7.2, 11.02) * mm, v(-7.18, 10.72) * mm, v(-7.17, 10.15) * mm], "startDerivative": vector(0.54, 0.03) * mm, "endDerivative": vector(0.01, -2.06) * mm});
            skFitSpline(sketch, "E155", {"points": [v(-7.17, 10.15) * mm, v(-7.32, 9.84) * mm, v(-7.58, 9.45) * mm, v(-7.89, 9.07) * mm, v(-8.28, 8.64) * mm, v(-8.62, 8.22) * mm, v(-8.71, 8.07) * mm, v(-8.72, 7.83) * mm, v(-8.7, 7.68) * mm, v(-8.63, 7.33) * mm, v(-8.66, 7.05) * mm, v(-8.94, 6.6) * mm, v(-9.23, 6.18) * mm, v(-9.62, 5.76) * mm, v(-9.94, 5.48) * mm, v(-10.16, 5.1) * mm, v(-10.35, 4.66) * mm, v(-10.58, 3.95) * mm, v(-10.64, 3.57) * mm, v(-10.65, 3.17) * mm, v(-10.64, 2.85) * mm, v(-10.79, 2.68) * mm, v(-11.06, 2.55) * mm, v(-11.2, 2.32) * mm, v(-11.4, 1.86) * mm, v(-11.57, 1.32) * mm, v(-11.8, 0.9) * mm, v(-12.16, 0.46) * mm, v(-12.29, 0.26) * mm, v(-12.45, -0.2) * mm, v(-12.58, -0.86) * mm, v(-12.92, -2.58) * mm, v(-12.96, -3.24) * mm, v(-12.73, -3.58) * mm, v(-12.62, -3.83) * mm, v(-12.7, -3.95) * mm, v(-12.87, -4.07) * mm, v(-12.96, -4.15) * mm, v(-12.96, -4.38) * mm, v(-12.94, -4.46) * mm, v(-12.85, -4.56) * mm, v(-12.75, -4.64) * mm, v(-12.6, -4.66) * mm, v(-12.47, -4.7) * mm, v(-12.4, -4.8) * mm, v(-12.38, -4.98) * mm, v(-12.4, -5.12) * mm, v(-12.47, -5.22) * mm, v(-12.6, -5.3) * mm, v(-12.67, -5.35) * mm, v(-12.73, -5.5) * mm, v(-12.74, -5.78) * mm, v(-12.74, -6.76) * mm, v(-12.76, -6.8) * mm, v(-12.87, -6.84) * mm, v(-13.02, -6.9) * mm, v(-13.04, -7) * mm, v(-13.03, -7.18) * mm, v(-12.99, -7.34) * mm, v(-12.88, -7.46) * mm, v(-12.67, -7.46) * mm], "startDerivative": vector(-7.63, -17.08) * mm, "endDerivative": vector(17.06, 2.75) * mm});
            skLineSegment(sketch, "E156", {"start": v(-12.67, -7.46) * mm, "end": v(-11.18, -7.4) * mm});
            skLineSegment(sketch, "E157", {"start": v(-11.18, -7.4) * mm, "end": v(-10.82, -7.84) * mm});
            skLineSegment(sketch, "E158", {"start": v(-10.82, -7.84) * mm, "end": v(-10.22, -7.84) * mm});
            skLineSegment(sketch, "E159", {"start": v(-10.22, -7.84) * mm, "end": v(-10.07, -7.52) * mm});
            skLineSegment(sketch, "E160", {"start": v(-9.4, -7.67) * mm, "end": v(-6.9, -7.67) * mm});
            skFitSpline(sketch, "E161", {"points": [v(-10.07, -7.52) * mm, v(-10, -7.44) * mm, v(-9.86, -7.36) * mm, v(-9.58, -7.33) * mm, v(-9.4, -7.36) * mm, v(-9.38, -7.44) * mm, v(-9.39, -7.6) * mm, v(-9.4, -7.67) * mm], "startDerivative": vector(0.55, 0.68) * mm, "endDerivative": vector(-0.09, -0.66) * mm});
            skFitSpline(sketch, "E162", {"points": [v(-6.9, -7.67) * mm, v(-6.87, -7.64) * mm, v(-6.86, -7.57) * mm, v(-6.87, -7.41) * mm, v(-6.86, -7.34) * mm, v(-6.8, -7.3) * mm, v(-6.71, -7.28) * mm, v(-6.49, -7.3) * mm, v(-6.3, -7.3) * mm, v(-6.25, -7.23) * mm, v(-6.22, -7.09) * mm], "startDerivative": vector(0.6, 0.42) * mm, "endDerivative": vector(0.21, 1.33) * mm});
            skLineSegment(sketch, "E163", {"start": v(-6.22, -7.09) * mm, "end": v(-6.22, -4.13) * mm});
            skLineSegment(sketch, "E164", {"start": v(-6.22, -4.13) * mm, "end": v(-5.7, -3.29) * mm});
            skLineSegment(sketch, "E165", {"start": v(-5.7, -3.29) * mm, "end": v(-5.72, -2.17) * mm});
            skFitSpline(sketch, "E166", {"points": [v(-5.72, -2.17) * mm, v(-5.88, -2.07) * mm, v(-6.11, -2.01) * mm, v(-6.3, -2.02) * mm, v(-6.38, -2.07) * mm, v(-6.42, -2.15) * mm, v(-6.41, -2.35) * mm, v(-6.42, -2.5) * mm, v(-6.42, -2.6) * mm, v(-6.5, -2.62) * mm, v(-6.67, -2.61) * mm, v(-6.7, -2.68) * mm, v(-6.67, -2.82) * mm, v(-6.66, -2.93) * mm, v(-6.74, -3) * mm, v(-6.95, -3) * mm, v(-7.28, -2.96) * mm, v(-7.46, -3) * mm, v(-7.54, -3.16) * mm, v(-7.53, -3.58) * mm, v(-7.7, -3.7) * mm, v(-8, -3.92) * mm, v(-8.29, -4.08) * mm, v(-8.63, -4.32) * mm, v(-8.89, -4.65) * mm, v(-9.03, -4.99) * mm, v(-9.24, -5.3) * mm, v(-9.55, -5.54) * mm, v(-9.97, -5.68) * mm, v(-10.34, -5.77) * mm, v(-10.6, -5.89) * mm, v(-11.03, -6.18) * mm, v(-11.28, -6.33) * mm, v(-11.47, -6.4) * mm, v(-11.6, -6.37) * mm, v(-11.68, -6.26) * mm, v(-11.71, -6.16) * mm, v(-11.71, -6.1) * mm], "startDerivative": vector(-5.87, 4.05) * mm, "endDerivative": vector(0.18, 3.44) * mm});
            skFitSpline(sketch, "E167", {"points": [v(-9.93, -0.9) * mm, v(-9.43, 0.18) * mm, v(-9.08, 0.7) * mm, v(-8.84, 0.71) * mm, v(-8.74, 0.83) * mm, v(-8.7, 1.08) * mm, v(-8.77, 1.67) * mm, v(-8.77, 1.9) * mm, v(-8.59, 2.18) * mm, v(-8.22, 2.46) * mm, v(-7.94, 2.5) * mm, v(-7.76, 2.62) * mm, v(-7.71, 2.8) * mm, v(-7.71, 3.38) * mm, v(-7.65, 3.82) * mm, v(-7.42, 4.24) * mm, v(-7.22, 4.52) * mm, v(-7.1, 5.22) * mm, v(-6.75, 5.8) * mm, v(-6.5, 6.34) * mm, v(-6.44, 6.73) * mm, v(-6.45, 7.09) * mm, v(-6.45, 7.24) * mm, v(-6.36, 7.35) * mm, v(-6.26, 7.46) * mm], "startDerivative": vector(6.85, 15.14) * mm, "endDerivative": vector(3.51, 4.44) * mm});
            skLineSegment(sketch, "E168", {"start": v(7.98, -5.24) * mm, "end": v(7.98, -0.07) * mm});
            skLineSegment(sketch, "E169", {"start": v(-2.61, 5.8) * mm, "end": v(-2.61, 6.7) * mm});
            skFitSpline(sketch, "E170", {"points": [v(-5.16, 9.13) * mm, v(-5.33, 9.04) * mm, v(-5.5, 8.98) * mm, v(-5.54, 8.79) * mm, v(-5.48, 8.58) * mm, v(-5.42, 8.29) * mm, v(-5.42, 7.9) * mm, v(-5.42, 7.6) * mm, v(-5.35, 7.37) * mm, v(-5.16, 7.33) * mm, v(-4.96, 7.42) * mm, v(-4.71, 7.56) * mm, v(-4.4, 7.73) * mm, v(-4.08, 8.1) * mm, v(-3.98, 8.62) * mm, v(-3.94, 9.27) * mm, v(-3.85, 9.8) * mm, v(-3.71, 10.37) * mm, v(-3.25, 10.87) * mm, v(-2.8, 10.94) * mm, v(-2.42, 10.92) * mm, v(-2.27, 10.7) * mm, v(-2.1, 10.54) * mm, v(-1.73, 10.5) * mm, v(-1.4, 10.62) * mm, v(-1.11, 10.58) * mm, v(-1.08, 10.37) * mm, v(-1.15, 9.7) * mm, v(-1.33, 9.3) * mm, v(-1.73, 8.67) * mm, v(-2.11, 8.02) * mm, v(-2.44, 7.25) * mm, v(-2.61, 6.7) * mm], "startDerivative": vector(-7.03, -4.8) * mm, "endDerivative": vector(-3.96, -13.87) * mm});
            skFitSpline(sketch, "E171", {"points": [v(-2.61, 5.8) * mm, v(-2.75, 5.54) * mm, v(-3.02, 5.23) * mm, v(-3.25, 4.89) * mm, v(-3.23, 4.52) * mm, v(-3.21, 4.2) * mm, v(-3.29, 3.94) * mm, v(-3.52, 3.8) * mm, v(-3.61, 3.54) * mm, v(-3.5, 3.33) * mm, v(-3.36, 3.1) * mm, v(-3.4, 2.8) * mm, v(-3.6, 2.44) * mm, v(-3.77, 2.18) * mm, v(-4.11, 1.23) * mm, v(-4.5, 0.14) * mm, v(-4.7, -0.84) * mm, v(-4.73, -1.67) * mm, v(-4.73, -2.3) * mm, v(-4.63, -3.38) * mm, v(-4.3, -4.11) * mm], "startDerivative": vector(-2.87, -6.96) * mm, "endDerivative": vector(6, -10.42) * mm});
            skLineSegment(sketch, "E172", {"start": v(-4.3, -4.11) * mm, "end": v(-4.3, -5.4) * mm});
            skFitSpline(sketch, "E173", {"points": [v(-4.3, -5.4) * mm, v(-4.4, -5.55) * mm, v(-4.46, -5.79) * mm, v(-4.42, -6.42) * mm, v(-4.44, -6.8) * mm, v(-4.61, -6.75) * mm, v(-4.71, -6.77) * mm, v(-4.73, -6.96) * mm, v(-4.7, -7.38) * mm, v(-4.73, -7.55) * mm, v(-4.96, -7.73) * mm, v(-5.25, -7.94) * mm, v(-5.2, -8.2) * mm, v(-5.04, -8.27) * mm, v(-5.04, -8.46) * mm, v(-5.13, -8.67) * mm, v(-5.27, -8.75) * mm, v(-5.44, -8.79) * mm], "startDerivative": vector(-2.05, -2.92) * mm, "endDerivative": vector(-3.47, -0.69) * mm});
            skFitSpline(sketch, "E174", {"points": [v(2.01, 13.02) * mm, v(2.29, 12.87) * mm, v(2.29, 12.57) * mm, v(2.12, 11.93) * mm, v(1.6, 11.2) * mm, v(1.42, 10.85) * mm, v(1.44, 10.28) * mm, v(1.32, 9.88) * mm, v(0.84, 9.63) * mm, v(0.77, 9.23) * mm, v(0.84, 8.73) * mm, v(0.6, 8.43) * mm, v(0.34, 8.43) * mm, v(0.2, 6.9) * mm, v(-0.08, 6.34) * mm, v(-0.22, 6.04) * mm], "startDerivative": vector(6.63, -2.08) * mm, "endDerivative": vector(-2.03, -5.56) * mm});
            skLineSegment(sketch, "E175", {"start": v(-0.22, 6.04) * mm, "end": v(-0.22, 3.53) * mm});
            skFitSpline(sketch, "E176", {"points": [v(-0.22, 3.53) * mm, v(-0.4, 3.3) * mm, v(-0.55, 2.8) * mm, v(-0.7, 2.21) * mm, v(-0.8, 1.96) * mm, v(-0.95, 1.78) * mm, v(-1.08, 1.62) * mm, v(-1.07, 1.22) * mm, v(-1.05, 0.9) * mm, v(-1.2, 0.67) * mm, v(-1.66, 0.22) * mm, v(-1.78, -0.17) * mm, v(-1.76, -0.93) * mm, v(-1.72, -2.02) * mm, v(-1.75, -2.69) * mm, v(-2.2, -3.64) * mm, v(-2.26, -3.84) * mm], "startDerivative": vector(-3.94, -4) * mm, "endDerivative": vector(-0.27, -3.88) * mm});
            skLineSegment(sketch, "E177", {"start": v(-2.26, -3.84) * mm, "end": v(-2.29, -5.41) * mm});
            skFitSpline(sketch, "E178", {"points": [v(-2.9, -6.7) * mm, v(-2.97, -6.83) * mm, v(-3, -6.99) * mm, v(-3.02, -7.06) * mm], "startDerivative": vector(-0.24, -0.34) * mm, "endDerivative": vector(-0.1, -0.25) * mm});
            skFitSpline(sketch, "E179", {"points": [v(-3.26, -7.56) * mm, v(-3.33, -7.69) * mm, v(-3.33, -7.88) * mm, v(-3.19, -8.02) * mm, v(-2.9, -8.04) * mm, v(-2.58, -8.08) * mm, v(-2.17, -8.02) * mm, v(-1.86, -7.94) * mm, v(-1.75, -7.88) * mm, v(-1.75, -7.32) * mm], "startDerivative": vector(-0.96, -1.46) * mm, "endDerivative": vector(-0.45, 4.47) * mm});
            skFitSpline(sketch, "E180", {"points": [v(1.04, -5.92) * mm, v(1.16, -5.74) * mm, v(1.27, -5.6) * mm, v(1.32, -5.48) * mm, v(1.42, -5.45) * mm, v(1.53, -5.52) * mm, v(1.6, -5.66) * mm, v(1.68, -5.68) * mm], "startDerivative": vector(0.68, 1.02) * mm, "endDerivative": vector(0.81, -0.05) * mm});
            skFitSpline(sketch, "E181", {"points": [v(2.76, -5.68) * mm, v(2.9, -5.85) * mm, v(3, -6.13) * mm, v(3, -6.4) * mm, v(2.97, -6.54) * mm, v(2.8, -6.54) * mm, v(2.71, -6.6) * mm, v(2.69, -6.8) * mm, v(2.72, -7.06) * mm, v(2.79, -7.23) * mm, v(2.9, -7.35) * mm], "startDerivative": vector(1.4, -1.36) * mm, "endDerivative": vector(1.38, -1.22) * mm});
            skFitSpline(sketch, "E182", {"points": [v(4.28, 13.32) * mm, v(3.9, 13.17) * mm, v(3.74, 12.84) * mm, v(3.76, 12.42) * mm, v(3.7, 12.03) * mm, v(3.38, 11.78) * mm, v(3.07, 11.53) * mm, v(3, 10.98) * mm, v(3.03, 10.61) * mm, v(2.84, 10.23) * mm, v(2.38, 9.4) * mm, v(2.26, 9.05) * mm, v(2.07, 8.73) * mm, v(1.93, 8.42) * mm, v(1.97, 8.11) * mm, v(2.05, 7.88) * mm, v(1.82, 7.63) * mm, v(1.45, 7.05) * mm, v(1.34, 6.28) * mm, v(1.3, 5.34) * mm, v(1.09, 5.03) * mm, v(0.82, 4.82) * mm, v(0.78, 4.55) * mm, v(0.84, 4.11) * mm, v(0.82, 3.78) * mm, v(0.55, 3.4) * mm, v(0.32, 3.07) * mm, v(0.22, 2.52) * mm, v(0.24, 1.7) * mm, v(0.3, 1.48) * mm, v(0.47, 1.38) * mm, v(0.59, 1.38) * mm, v(0.63, 1.25) * mm, v(0.47, 1.23) * mm, v(0.32, 1.15) * mm, v(0.24, 0.98) * mm, v(0.28, 0.13) * mm, v(0, -0.23) * mm, v(0, -0.66) * mm, v(0, -1.02) * mm, v(0, -1.5) * mm, v(0, -1.9) * mm, v(0, -2.5) * mm, v(-0.28, -2.77) * mm, v(-0.72, -3.06) * mm, v(-0.78, -3.35) * mm, v(-0.74, -3.87) * mm, v(-0.97, -4.08) * mm, v(-1.32, -4.3) * mm, v(-1.45, -4.58) * mm, v(-1.37, -5.21) * mm, v(-1.2, -5.48) * mm, v(-0.72, -5.48) * mm, v(-0.2, -5.14) * mm, v(0.57, -4.75) * mm, v(1.17, -4.6) * mm, v(1.78, -4.68) * mm, v(2.45, -4.7) * mm, v(2.95, -4.44) * mm, v(3.03, -3.94) * mm, v(2.7, -3.71) * mm, v(2.36, -3.44) * mm, v(2.24, -3.16) * mm, v(2.36, -2.6) * mm, v(2.32, -2.27) * mm, v(2.2, -2.08) * mm, v(2.3, -1.87) * mm, v(2.4, -1.8) * mm], "startDerivative": vector(-28.95, -7) * mm, "endDerivative": vector(10.76, 7.4) * mm});
            skFitSpline(sketch, "E183", {"points": [v(4.59, -3.02) * mm, v(4.82, -3.21) * mm, v(5.03, -3.73) * mm, v(4.95, -4.27) * mm, v(4.7, -5.04) * mm, v(4.4, -5.68) * mm, v(4, -6.21) * mm, v(3.74, -6.62) * mm, v(3.68, -7) * mm, v(3.78, -7.39) * mm, v(4.09, -7.7) * mm, v(4.59, -8.08) * mm, v(4.8, -8.46) * mm, v(4.74, -8.87) * mm, v(4.95, -9.83) * mm, v(5.3, -10.77) * mm, v(5.34, -11.44) * mm, v(5.3, -12.3) * mm, v(5.57, -12.44) * mm, v(5.93, -12.29) * mm, v(6.05, -12.1) * mm, v(6.07, -11.8) * mm, v(6.01, -11.29) * mm, v(6.03, -11.08) * mm, v(6.24, -10.89) * mm, v(6.3, -10.23) * mm, v(6.63, -9.3) * mm, v(6.88, -8.75) * mm, v(6.84, -8.2) * mm, v(6.82, -7.66) * mm, v(7.13, -7.37) * mm, v(7.28, -7.1) * mm, v(7.36, -6.54) * mm, v(7.57, -6.04) * mm, v(7.76, -5.56) * mm, v(7.98, -5.24) * mm], "startDerivative": vector(10.71, -7.06) * mm, "endDerivative": vector(9.38, 11.88) * mm});
            skFitSpline(sketch, "E184", {"points": [v(4.28, 13.32) * mm, v(4.59, 13.32) * mm, v(4.8, 12.98) * mm, v(4.82, 12.42) * mm, v(4.9, 12.03) * mm, v(5.24, 11.48) * mm, v(5.59, 11.01) * mm, v(5.74, 10.65) * mm, v(5.72, 10.23) * mm, v(5.72, 9.76) * mm, v(6.1, 8.53) * mm, v(6.43, 7.61) * mm, v(6.6, 7.01) * mm, v(6.68, 6.36) * mm, v(6.82, 5.73) * mm, v(7.09, 5.02) * mm, v(7.26, 4.92) * mm, v(7.3, 4.67) * mm, v(7.18, 4.15) * mm, v(7.47, 3.67) * mm, v(7.65, 3.23) * mm, v(7.65, 2.28) * mm, v(7.72, 0.86) * mm, v(7.98, -0.07) * mm], "startDerivative": vector(10.5, 2.13) * mm, "endDerivative": vector(5.29, -15.56) * mm});
            skFitSpline(sketch, "E185", {"points": [v(6.1, 13.21) * mm, v(6.03, 13.12) * mm, v(6.1, 12.95) * mm, v(6.36, 12.8) * mm, v(6.76, 12.76) * mm, v(7.3, 12.53) * mm, v(7.81, 12.1) * mm, v(8.17, 11.52) * mm, v(8.43, 11.03) * mm, v(8.62, 11.04) * mm, v(8.89, 11.25) * mm, v(9.18, 11.29) * mm, v(9.4, 11.23) * mm, v(9.55, 11.06) * mm, v(9.52, 10.9) * mm, v(9.43, 10.8) * mm], "startDerivative": vector(-1.99, -2.1) * mm, "endDerivative": vector(-2.27, -2.06) * mm});
            skFitSpline(sketch, "E186", {"points": [v(8, 9.73) * mm, v(7.76, 9.53) * mm, v(7.54, 9) * mm, v(7.76, 8.23) * mm, v(8, 7.2) * mm, v(8.17, 5.89) * mm, v(8.22, 4.77) * mm, v(8.5, 4.07) * mm, v(8.47, 3.2) * mm, v(8.6, 3) * mm, v(8.82, 2.32) * mm, v(8.95, 1.52) * mm, v(8.95, 1.3) * mm], "startDerivative": vector(-4.19, -3.01) * mm, "endDerivative": vector(-0.24, -4.06) * mm});
            skFitSpline(sketch, "E187", {"points": [v(9.02, -4.44) * mm, v(9.17, -4.62) * mm, v(9.32, -4.76) * mm, v(9.32, -5) * mm], "startDerivative": vector(0.4, -0.6) * mm, "endDerivative": vector(-0.14, -0.8) * mm});
            skFitSpline(sketch, "E188", {"points": [v(8.14, -7.99) * mm, v(8.14, -8.26) * mm, v(8.14, -8.58) * mm, v(8.61, -8.95) * mm, v(9.19, -9.37) * mm, v(9.92, -9.9) * mm, v(10.34, -10.53) * mm, v(10.78, -11.32) * mm, v(11.1, -12.05) * mm, v(11.2, -11.91) * mm, v(11.3, -11.6) * mm, v(11.26, -10.76) * mm, v(11.26, -10.28) * mm, v(11.5, -9.97) * mm, v(11.5, -9.47) * mm, v(11.53, -8.41) * mm, v(11.23, -7.99) * mm, v(11.23, -7.58) * mm, v(11.42, -7.1) * mm, v(11.46, -6.43) * mm, v(11.42, -5.56) * mm, v(11.24, -5.34) * mm, v(11.13, -5.1) * mm, v(11.15, -5) * mm, v(11.46, -4.84) * mm, v(11.47, -4.44) * mm], "startDerivative": vector(0.62, -8.87) * mm, "endDerivative": vector(-2.57, 12.74) * mm});
            skLineSegment(sketch, "E189", {"start": v(11.47, -4.44) * mm, "end": v(10.93, 0.57) * mm});
            skFitSpline(sketch, "E190", {"points": [v(11.43, 1.89) * mm, v(11.49, 1.95) * mm, v(11.56, 1.92) * mm, v(11.61, 1.83) * mm], "startDerivative": vector(0.16, 0.24) * mm, "endDerivative": vector(0.11, -0.26) * mm});
            skFitSpline(sketch, "E191", {"points": [v(12.27, 0.9) * mm, v(12.42, 0.62) * mm, v(12.55, 0.24) * mm, v(12.46, -0.32) * mm, v(12.34, -0.88) * mm, v(12.34, -1.3) * mm, v(12.62, -1.47) * mm, v(12.98, -2.26) * mm, v(13.23, -3.5) * mm, v(13.5, -5.07) * mm, v(13.56, -6.45) * mm, v(13.58, -7.32) * mm, v(13.17, -8.35) * mm, v(12.73, -9.35) * mm, v(12.67, -9.84) * mm, v(12.83, -9.97) * mm, v(13.62, -10) * mm, v(14.16, -10.32) * mm, v(14.73, -11) * mm, v(15.29, -11.4) * mm, v(15.71, -11.57) * mm, v(15.98, -11.47) * mm, v(16.1, -11.1) * mm, v(16.25, -10.4) * mm, v(16.42, -9.07) * mm, v(16.52, -8.12) * mm, v(16.54, -7.09) * mm, v(16.58, -6.03) * mm, v(16.46, -5.41) * mm, v(16.1, -5.24) * mm, v(15.87, -5.22) * mm, v(15.84, -5.06) * mm, v(15.94, -4.85) * mm, v(16.14, -4.6) * mm, v(16.14, -4.2) * mm, v(16.03, -3.37) * mm, v(15.94, -2.06) * mm, v(15.87, -1.9) * mm, v(15.64, -1.85) * mm, v(15.45, -1.7) * mm, v(15.3, -1.4) * mm, v(15.28, -1) * mm, v(15.25, 0.9) * mm, v(15.09, 1.55) * mm, v(14.8, 2) * mm, v(14.53, 2.03) * mm, v(14.48, 2.1) * mm, v(14.54, 2.27) * mm, v(14.63, 2.4) * mm, v(14.59, 2.6) * mm, v(13.42, 3.52) * mm, v(13.3, 3.5) * mm, v(13.17, 3.45) * mm, v(13.04, 3.46) * mm, v(12.97, 3.57) * mm, v(12.97, 3.71) * mm, v(12.98, 3.88) * mm, v(13.04, 3.97) * mm, v(13.25, 4.05) * mm, v(13.78, 4.22) * mm, v(14.4, 4.77) * mm, v(15.03, 5.81) * mm, v(15.35, 6.68) * mm, v(15.34, 7.17) * mm, v(15.3, 7.56) * mm, v(15.48, 8.25) * mm, v(15.64, 8.88) * mm, v(15.57, 9.53) * mm, v(15.14, 10.58) * mm, v(14.4, 11.72) * mm, v(13.7, 12.36) * mm, v(13.22, 12.56) * mm], "startDerivative": vector(14, -24.92) * mm, "endDerivative": vector(-33.86, 10.62) * mm});
            skFitSpline(sketch, "E192", {"points": [v(9.16, 13.21) * mm, v(9.3, 13.29) * mm, v(9.43, 13.4) * mm, v(9.6, 13.45) * mm, v(9.75, 13.32) * mm, v(9.9, 13.21) * mm, v(10, 13.08) * mm], "startDerivative": vector(0.91, 0.4) * mm, "endDerivative": vector(0.58, -0.9) * mm});
            skFitSpline(sketch, "E193", {"points": [v(10.74, 10.42) * mm, v(10.74, 10.55) * mm, v(10.74, 10.68) * mm, v(10.98, 10.68) * mm, v(11.42, 10.57) * mm, v(11.61, 10.36) * mm, v(11.89, 10.05) * mm, v(12.27, 9.68) * mm, v(12.73, 9.18) * mm, v(13.08, 8.68) * mm, v(13.17, 8.45) * mm, v(13.12, 7.43) * mm, v(13.05, 7.12) * mm, v(12.92, 6.84) * mm, v(12.9, 6.45) * mm, v(12.9, 6.17) * mm, v(12.78, 5.93) * mm, v(12.63, 5.69) * mm, v(12.54, 5.48) * mm, v(12.46, 5.14) * mm, v(12.4, 4.96) * mm, v(12.12, 4.68) * mm, v(11.78, 4.44) * mm, v(11.52, 4.3) * mm, v(10.94, 4.29) * mm, v(10.82, 4.37) * mm, v(10.74, 4.5) * mm, v(10.74, 4.64) * mm], "startDerivative": vector(0.4, 5.1) * mm, "endDerivative": vector(0.83, 5.72) * mm});
            skFitSpline(sketch, "E194", {"points": [v(16.16, 13.7) * mm, v(15.72, 13.77) * mm, v(15.25, 13.77) * mm, v(14.96, 13.77) * mm, v(14.97, 13.58) * mm, v(15.2, 13.3) * mm, v(15.63, 12.92) * mm, v(16, 12.56) * mm, v(16.48, 12.2) * mm, v(16.73, 12) * mm, v(16.8, 11.73) * mm, v(16.82, 11.2) * mm, v(16.78, 10.55) * mm, v(16.72, 10.37) * mm, v(16.66, 10.27) * mm], "startDerivative": vector(-5.58, 1.1) * mm, "endDerivative": vector(-1.5, -2.44) * mm});
            skLineSegment(sketch, "E195", {"start": v(16.66, 10.27) * mm, "end": v(16.71, 8.94) * mm});
            skLineSegment(sketch, "E196", {"start": v(16.71, 8.94) * mm, "end": v(16.4, 8.71) * mm});
            skFitSpline(sketch, "E197", {"points": [v(17.05, -1.14) * mm, v(17.05, -1.4) * mm, v(17.29, -1.7) * mm, v(17.56, -2.2) * mm, v(17.8, -2.68) * mm, v(17.86, -3.1) * mm], "startDerivative": vector(-0.32, -1.77) * mm, "endDerivative": vector(0.18, -2.1) * mm});
            skFitSpline(sketch, "E198", {"points": [v(17.5, -6.18) * mm, v(17.5, -6.46) * mm, v(17.5, -6.77) * mm, v(17.74, -7.13) * mm, v(17.95, -7.54) * mm, v(18, -7.87) * mm, v(18.06, -8.02) * mm, v(18.24, -8.17) * mm, v(18.3, -8.27) * mm, v(18.2, -8.4) * mm, v(17.86, -8.64) * mm, v(17.5, -8.75) * mm, v(17.37, -8.88) * mm, v(17.56, -9.3) * mm, v(17.72, -9.67) * mm, v(17.73, -10.17) * mm, v(17.55, -10.6) * mm, v(17.5, -10.8) * mm, v(17.33, -11.09) * mm, v(17.05, -11.33) * mm, v(16.92, -11.51) * mm, v(17.05, -11.7) * mm, v(17.5, -11.68) * mm, v(18, -11.63) * mm, v(18.3, -11.55) * mm, v(18.43, -11.4) * mm, v(18.67, -11.35) * mm, v(18.98, -11.37) * mm, v(19.12, -11.49) * mm, v(19.22, -11.61) * mm, v(19.41, -11.63) * mm, v(19.5, -11.53) * mm, v(19.69, -11.37) * mm, v(19.96, -11.33) * mm, v(21.29, -11.03) * mm, v(22, -10.47) * mm, v(22.49, -9.6) * mm, v(22.64, -8.77) * mm, v(22.67, -7.93) * mm, v(22.7, -7.88) * mm, v(22.8, -7.8) * mm, v(22.9, -7.67) * mm], "startDerivative": vector(0.56, -12.51) * mm, "endDerivative": vector(5.16, 8.04) * mm});
            skFitSpline(sketch, "E199", {"points": [v(19.41, -7.54) * mm, v(19.41, -7.72) * mm, v(19.47, -7.88) * mm, v(19.56, -7.96) * mm, v(19.71, -7.88) * mm, v(19.9, -7.61) * mm, v(20.05, -7.23) * mm, v(20.3, -6.64) * mm, v(20.44, -6.24) * mm, v(20.48, -5.7) * mm, v(20.57, -5.29) * mm, v(20.76, -4.86) * mm, v(20.99, -4.38) * mm, v(21.16, -3.83) * mm, v(21.19, -3.56) * mm], "startDerivative": vector(-0.24, -3.55) * mm, "endDerivative": vector(0.26, 3.84) * mm});
            skFitSpline(sketch, "E200", {"points": [v(19.53, 1.66) * mm, v(19.41, 1.95) * mm, v(19.21, 2.07) * mm, v(19.29, 2.4) * mm, v(19.11, 2.94) * mm, v(18.89, 3.6) * mm], "startDerivative": vector(-0.33, 1.97) * mm, "endDerivative": vector(-0.76, 2.55) * mm});
            skLineSegment(sketch, "E201", {"start": v(18.89, 3.6) * mm, "end": v(18.79, 7.74) * mm});
            skFitSpline(sketch, "E202", {"points": [v(18.79, 7.74) * mm, v(18.81, 7.82) * mm, v(18.86, 7.89) * mm, v(18.93, 7.93) * mm, v(18.97, 7.94) * mm], "startDerivative": vector(0.06, 0.3) * mm, "endDerivative": vector(0.21, 0) * mm});
            skFitSpline(sketch, "E203", {"points": [v(19.83, 7.94) * mm, v(20.25, 7.85) * mm, v(20.62, 7.57) * mm, v(20.9, 7.19) * mm, v(21.2, 6.9) * mm, v(21.55, 6.54) * mm, v(21.9, 5.93) * mm, v(22.14, 5.25) * mm, v(22.2, 3.87) * mm, v(22.12, 3.22) * mm, v(21.8, 2.54) * mm, v(21.72, 2.18) * mm, v(21.7, 1.9) * mm, v(21.59, 1.64) * mm, v(21.37, 1.26) * mm, v(21.24, 0.97) * mm], "startDerivative": vector(7.1, -0.7) * mm, "endDerivative": vector(-2.24, -5.27) * mm});
            skFitSpline(sketch, "E204", {"points": [v(22.9, -5.97) * mm, v(23.02, -5.7) * mm, v(23.2, -5.4) * mm, v(23.17, -4.92) * mm, v(23.17, -3.94) * mm, v(23.1, -2.94) * mm, v(23.1, -1.13) * mm, v(23.2, -0.34) * mm, v(23.29, 0.12) * mm, v(23.42, 0.37) * mm, v(23.71, 0.54) * mm, v(23.87, 0.97) * mm, v(23.98, 1.29) * mm], "startDerivative": vector(1.85, 4.44) * mm, "endDerivative": vector(1.92, 4.56) * mm});
            skFitSpline(sketch, "E205", {"points": [v(23.95, 6.74) * mm, v(24.12, 6.46) * mm, v(24.27, 6.12) * mm, v(24.3, 5.4) * mm, v(24.35, 4.29) * mm, v(24.29, 3.64) * mm, v(24.27, 3.37) * mm, v(24.1, 3.06) * mm, v(23.95, 2.85) * mm, v(23.92, 2.6) * mm], "startDerivative": vector(1.73, -2.93) * mm, "endDerivative": vector(0, -3.13) * mm});
            skFitSpline(sketch, "E206", {"points": [v(16.16, 13.7) * mm, v(16.36, 13.55) * mm, v(16.65, 13.52) * mm, v(17.01, 13.52) * mm, v(17.53, 13.2) * mm, v(18.05, 12.94) * mm, v(18.26, 12.75) * mm, v(18.41, 12.6) * mm, v(18.84, 12.44) * mm, v(19.4, 12.25) * mm, v(19.66, 12.28) * mm, v(19.86, 12.36) * mm, v(20.2, 12.28) * mm, v(21.01, 12.03) * mm, v(21.2, 11.82) * mm, v(22.1, 11.7) * mm, v(22.43, 11.42) * mm, v(22.88, 11.03) * mm, v(23.14, 10.84) * mm, v(23.38, 10.44) * mm, v(23.47, 9.92) * mm, v(23.78, 9.27) * mm, v(23.9, 8.97) * mm], "startDerivative": vector(5.27, -5.14) * mm, "endDerivative": vector(2.35, -6.66) * mm});
            skFitSpline(sketch, "E207", {"points": [v(-5, 13.02) * mm, v(-5.1, 13) * mm, v(-5.17, 12.94) * mm, v(-5.2, 12.84) * mm, v(-5.23, 12.65) * mm], "startDerivative": vector(-0.47, -0.05) * mm, "endDerivative": vector(-0.07, -0.67) * mm});
            skLineSegment(sketch, "E208", {"start": v(-6.45, 12.8) * mm, "end": v(-6.45, 11.53) * mm});
            skLineSegment(sketch, "E209", {"start": v(-6.45, 11.53) * mm, "end": v(-6.26, 11.4) * mm});
            skFitSpline(sketch, "E210", {"points": [v(-5.44, -10.1) * mm, v(-5.32, -10.36) * mm, v(-5.05, -10.46) * mm, v(-4.52, -10.39) * mm, v(-4.2, -10.21) * mm, v(-3.81, -10.09) * mm], "startDerivative": vector(0.48, -1.72) * mm, "endDerivative": vector(1.94, 0.5) * mm});
            skFitSpline(sketch, "E211", {"points": [v(-2.26, -10.09) * mm, v(-2.05, -10.03) * mm, v(-1.84, -9.88) * mm, v(-1.58, -9.7) * mm, v(-1.32, -9.58) * mm, v(-0.92, -9.58) * mm, v(-0.48, -9.66) * mm, v(-0.37, -9.77) * mm, v(-0.37, -9.87) * mm, v(-0.26, -9.88) * mm], "startDerivative": vector(2, 0.4) * mm, "endDerivative": vector(1.88, 0.18) * mm});
            skArc(sketch, "E212", {"start": v(2.61, -9.88) * mm, "mid": v(2.81, -9.82) * mm, "end": v(2.9, -9.62) * mm});
            skLineSegment(sketch, "E213", {"start": v(-21.46, 5.83) * mm, "end": v(-21.18, 5.56) * mm});
            skLineSegment(sketch, "E214", {"start": v(9.3, -5.1) * mm, "end": v(9.32, -5) * mm});
            skLineSegment(sketch, "E215", {"start": v(-14.78, -0.74) * mm, "end": v(-15.23, -1.21) * mm});
            skLineSegment(sketch, "E216", {"start": v(5.24, 2.67) * mm, "end": v(5.45, 2.52) * mm});
            skSolve(sketch);
        }
        {
            var Q0;
            Q0=qSketchRegion(id+"F0",true);
            extrude(context, id + "F1", {"entities" : qUnion([Q0]), "depth" : 5 * mm, "offsetDistance" : 25 * mm});
        }
        {
            var Q0;
            Q0=makeQuery(id+"F1.opExtrude","CAP_FACE",FACE,{"disambiguationData":[OSD([sQuery(id+"F0.wireOp",EDGE,"E38"),sQuery(id+"F0.wireOp",EDGE,"E39"),sQuery(id+"F0.wireOp",EDGE,"E40"),sQuery(id+"F0.wireOp",EDGE,"E41"),sQuery(id+"F0.wireOp",EDGE,"E42"),sQuery(id+"F0.wireOp",EDGE,"E43"),sQuery(id+"F0.wireOp",EDGE,"E44"),sQuery(id+"F0.wireOp",EDGE,"E45"),sQuery(id+"F0.wireOp",EDGE,"E46"),sQuery(id+"F0.wireOp",EDGE,"E47"),sQuery(id+"F0.wireOp",EDGE,"E48"),sQuery(id+"F0.wireOp",EDGE,"E49"),sQuery(id+"F0.wireOp",EDGE,"E50"),sQuery(id+"F0.wireOp",EDGE,"E51"),sQuery(id+"F0.wireOp",EDGE,"E52"),sQuery(id+"F0.wireOp",EDGE,"E53"),sQuery(id+"F0.wireOp",EDGE,"E54"),sQuery(id+"F0.wireOp",EDGE,"E55"),sQuery(id+"F0.wireOp",EDGE,"E106"),sQuery(id+"F0.wireOp",EDGE,"E168"),sQuery(id+"F0.wireOp",EDGE,"E182"),sQuery(id+"F0.wireOp",EDGE,"E183"),sQuery(id+"F0.wireOp",EDGE,"E184"),sQuery(id+"F0.wireOp",EDGE,"E216")])],"isStart":true});
            var sketch = newSketch(context, id + "F2", { "sketchPlane" : qUnion([Q0])});
            skLineSegment(sketch, "E217.bottom", {"start": v(-38.04, -17.37) * mm, "end": v(30.08, -17.37) * mm});
            skLineSegment(sketch, "E217.top", {"start": v(-43.04, 17.59) * mm, "end": v(35.08, 17.59) * mm});
            skLineSegment(sketch, "E217.left", {"start": v(-43.04, -12.37) * mm, "end": v(-43.04, 17.59) * mm});
            skLineSegment(sketch, "E217.right", {"start": v(35.08, -12.37) * mm, "end": v(35.08, 17.59) * mm});
            skPoint(sketch, "E218.visualSharp", {"position": v(-43.04, -17.37) * mm});
            skArc(sketch, "E218.filletArc", {"start": v(-43.04, -12.37) * mm, "mid": v(-41.58, -15.9) * mm, "end": v(-38.04, -17.37) * mm});
            skPoint(sketch, "E219.visualSharp", {"position": v(35.08, -17.37) * mm});
            skArc(sketch, "E219.filletArc", {"start": v(30.08, -17.37) * mm, "mid": v(33.62, -15.9) * mm, "end": v(35.08, -12.37) * mm});
            skPoint(sketch, "E220.visualSharp", {"position": v(-43.04, 17.59) * mm});
            skSolve(sketch);
        }
        {
            var Q0;
            Q0=qSketchRegion(id+"F2",true);
            extrude(context, id + "F3", {"entities" : qUnion([Q0]), "operationType" : NewBodyOperationType.ADD, "depth" : 3.5 * mm, "offsetDistance" : 25 * mm});
        }
        {
            var Q0;
            Q0=makeQuery(id+"F3.opExtrude","CAP_FACE",FACE,{"disambiguationData":[OSD([sQuery(id+"F2.wireOp",EDGE,"E217.bottom"),sQuery(id+"F2.wireOp",EDGE,"E217.top"),sQuery(id+"F2.wireOp",EDGE,"E217.left"),sQuery(id+"F2.wireOp",EDGE,"E217.right"),sQuery(id+"F2.wireOp",EDGE,"E218.filletArc"),sQuery(id+"F2.wireOp",EDGE,"E219.filletArc"),sQuery(id+"F2.wireOp",EDGE,"744ff583-1bf7-4c06-8853-35fc34389462.filletArc"),sQuery(id+"F2.wireOp",EDGE,"E220.filletArc")])],"isStart":true});
            var sketch = newSketch(context, id + "F4", { "sketchPlane" : qUnion([Q0])});
            skLineSegment(sketch, "E221", {"start": v(-43.04, -17.59) * mm, "end": v(-19.7, -40.94) * mm});
            skLineSegment(sketch, "E222", {"start": v(35.08, -17.59) * mm, "end": v(11.73, -40.94) * mm});
            skLineSegment(sketch, "E223", {"start": v(-14.74, -42.99) * mm, "end": v(6.78, -42.99) * mm});
            skPoint(sketch, "E224.visualSharp", {"position": v(-17.64, -42.99) * mm});
            skArc(sketch, "E224.filletArc", {"start": v(-19.7, -40.94) * mm, "mid": v(-17.42, -42.45) * mm, "end": v(-14.74, -42.99) * mm});
            skPoint(sketch, "E225.visualSharp", {"position": v(9.68, -42.99) * mm});
            skArc(sketch, "E225.filletArc", {"start": v(6.78, -42.99) * mm, "mid": v(9.46, -42.45) * mm, "end": v(11.73, -40.94) * mm});
            skLineSegment(sketch, "E226", {"start": v(-43.04, -17.59) * mm, "end": v(35.08, -17.59) * mm});
            skSolve(sketch);
        }
        {
            var Q0;
            Q0=qSketchRegion(id+"F4",true);
            extrude(context, id + "F5", {"entities" : qUnion([Q0]), "operationType" : NewBodyOperationType.ADD, "oppositeDirection" : true, "depth" : 3.5 * mm, "offsetDistance" : 25 * mm});
        }
        {
            var Q0;
            {var subQ0=sQuery(id+"F2.wireOp",EDGE,"E217.left");Q0=makeQuery(id+"F5.boolean.opBoolean","MERGE",EDGE,{"derivedFrom":[makeQuery(id+"F3.opExtrude","SWEPT_EDGE",EDGE,{"disambiguationData":[OSD([sQuery(id+"F2.wireOp",EDGE,"E217.top"),subQ0])]}),makeQuery(id+"F5.opExtrude","SWEPT_EDGE",EDGE,{"disambiguationData":[OSD([subQ0,sQuery(id+"F4.wireOp",EDGE,"E221"),sQuery(id+"F4.wireOp",EDGE,"E226")])]})]});}
            var Q1;
            {var subQ0=sQuery(id+"F2.wireOp",EDGE,"E217.right");Q1=makeQuery(id+"F5.boolean.opBoolean","MERGE",EDGE,{"derivedFrom":[makeQuery(id+"F3.opExtrude","SWEPT_EDGE",EDGE,{"disambiguationData":[OSD([sQuery(id+"F2.wireOp",EDGE,"E217.top"),subQ0])]}),makeQuery(id+"F5.opExtrude","SWEPT_EDGE",EDGE,{"disambiguationData":[OSD([subQ0,sQuery(id+"F4.wireOp",EDGE,"E222"),sQuery(id+"F4.wireOp",EDGE,"E226")])]})]});}
            fillet(context, id + "F6", {"entities" : qUnion([Q0, Q1]), "radius" : 5 * mm, "tangentPropagation" : true, "allowEdgeOverflow" : false});
        }
        {
            var Q0;
            Q0=makeQuery(id+"F5.boolean.opBoolean","MERGE",FACE,{"derivedFrom":[makeQuery(id+"F3.opExtrude","CAP_FACE",FACE,{"disambiguationData":[OSD([sQuery(id+"F2.wireOp",EDGE,"E217.bottom"),sQuery(id+"F2.wireOp",EDGE,"E217.top"),sQuery(id+"F2.wireOp",EDGE,"E217.left"),sQuery(id+"F2.wireOp",EDGE,"E217.right"),sQuery(id+"F2.wireOp",EDGE,"E218.filletArc"),sQuery(id+"F2.wireOp",EDGE,"E219.filletArc")])],"isStart":true}),makeQuery(id+"F5.opExtrude","CAP_FACE",FACE,{"disambiguationData":[OSD([sQuery(id+"F4.wireOp",EDGE,"E221"),sQuery(id+"F4.wireOp",EDGE,"E222"),sQuery(id+"F4.wireOp",EDGE,"E223"),sQuery(id+"F4.wireOp",EDGE,"E224.filletArc"),sQuery(id+"F4.wireOp",EDGE,"E225.filletArc"),sQuery(id+"F4.wireOp",EDGE,"E226")])],"isStart":true})]});
            var sketch = newSketch(context, id + "F7", { "sketchPlane" : qUnion([Q0])});
            skEllipse(sketch, "E227", {"center": v(-3.98, -29.25) * mm, "majorRadius": 7.5 * mm, "minorRadius": 4.5 * mm, "majorAxis": v(1, 0)});
            skSolve(sketch);
        }
        {
            var Q0;
            Q0=qSketchRegion(id+"F7",true);
            extrude(context, id + "F8", {"entities" : qUnion([Q0]), "operationType" : NewBodyOperationType.ADD, "depth" : 20 * mm, "offsetDistance" : 25 * mm});
        }
        {
            var Q0;
            Q0=qCreatedBy(makeId("Right.planeOp"),FACE);
            var sketch = newSketch(context, id + "F9", { "sketchPlane" : qUnion([Q0])});
            skArc(sketch, "E228", {"start": v(-9.73, 10.61) * mm, "mid": v(-28.2, 14.58) * mm, "end": v(-14.6, 1.47) * mm});
            skLineSegment(sketch, "E229.bottom", {"start": v(-9.73, 10.61) * mm, "end": v(-14.6, 10.61) * mm});
            skLineSegment(sketch, "E229.right", {"start": v(-14.6, 10.61) * mm, "end": v(-14.6, 1.47) * mm});
            skSolve(sketch);
        }
        {
            var Q0;
            Q0=qSketchRegion(id+"F9",true);
            extrude(context, id + "F10", {"entities" : qUnion([Q0]), "operationType" : NewBodyOperationType.REMOVE, "endBound" : BoundingType.THROUGH_ALL, "oppositeDirection" : true, "depth" : 25 * mm, "offsetDistance" : 25 * mm});
        }
        {
            var Q0;
            Q0=qSketchRegion(id+"F9",true);
            extrude(context, id + "F11", {"entities" : qUnion([Q0]), "operationType" : NewBodyOperationType.REMOVE, "depth" : 25 * mm, "offsetDistance" : 25 * mm});
        }
        {
            var Q0;
            Q0=makeQuery(id+"F11.boolean.opBoolean","INTERSECT",EDGE,{"derivedFrom":[makeQuery(id+"F8.opExtrude","SWEPT_FACE",FACE,{"disambiguationData":[OSD([sQuery(id+"F7.wireOp",EDGE,"E227")])]}),makeQuery(id+"F11.opExtrude","SWEPT_FACE",FACE,{"disambiguationData":[OSD([sQuery(id+"F9.wireOp",EDGE,"E228")])]})]});
            var Q1;
            Q1=makeQuery(id+"F8.opExtrude","CAP_EDGE",EDGE,{"disambiguationData":[OSD([sQuery(id+"F7.wireOp",EDGE,"E227")])],"isStart":false});
            var Q2;
            Q2=makeQuery(id+"F5.opExtrude","CAP_EDGE",EDGE,{"disambiguationData":[OSD([sQuery(id+"F4.wireOp",EDGE,"E221")])],"isStart":true});
            fillet(context, id + "F12", {"entities" : qUnion([Q0, Q1, Q2]), "radius" : 1 * mm, "tangentPropagation" : true, "allowEdgeOverflow" : false});
        }
        {
            var Q0;
            Q0=makeQuery(id+"F3.opExtrude","CAP_EDGE",EDGE,{"disambiguationData":[OSD([sQuery(id+"F2.wireOp",EDGE,"E217.bottom")])],"isStart":false});
            fillet(context, id + "F13", {"entities" : qUnion([Q0]), "radius" : 1 * mm, "tangentPropagation" : true, "allowEdgeOverflow" : false});
        }
    });
